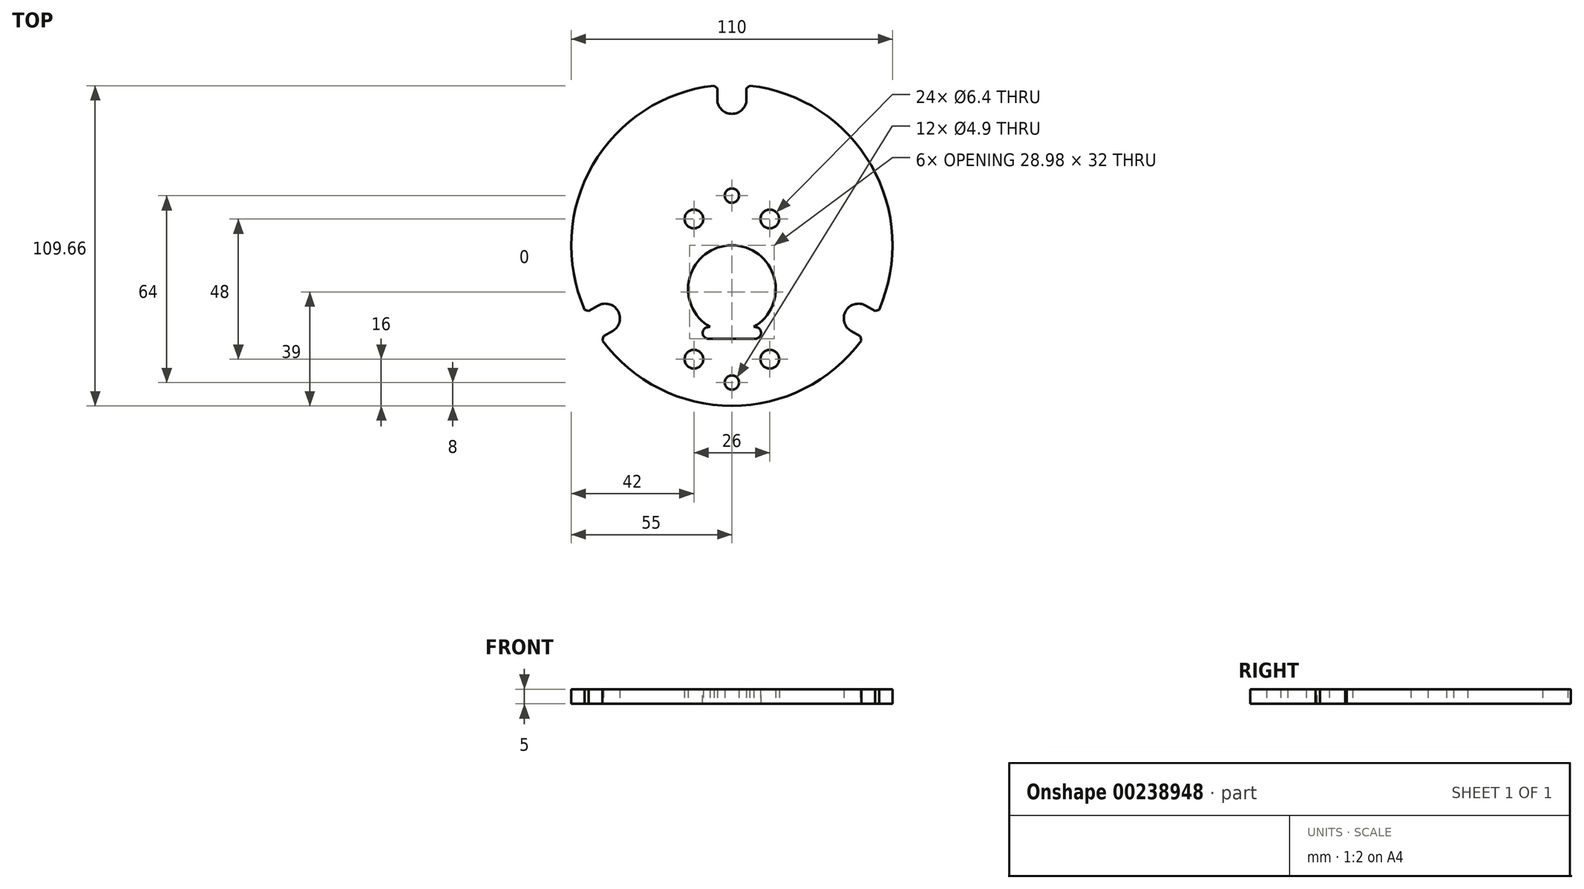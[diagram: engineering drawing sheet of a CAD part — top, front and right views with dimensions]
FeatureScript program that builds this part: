
annotation { "Feature Type Name" : "Feature", "Feature Type Description" : "" }
export const myFeature = defineFeature(function(context is Context, id is Id, definition is map)
    precondition{}
    {
        {
            var Q0;
            Q0=qCreatedBy(makeId("Top.planeOp"),FACE);
            var sketch = newSketch(context, id + "F0", { "sketchPlane" : qUnion([Q0])});
            skCircle(sketch, "E0", {"center": v(0, 0) * mm, "radius": 95 * mm, "construction": true});
            skPoint(sketch, "E1", {"position": v(0, -15) * mm});
            skPoint(sketch, "E2", {"position": v(0, 15) * mm});
            skCircle(sketch, "E3", {"center": v(0, 15) * mm, "radius": 80 * mm, "construction": true});
            skCircle(sketch, "E4", {"center": v(0, 15) * mm, "radius": 70 * mm, "construction": true});
            skLineSegment(sketch, "E5", {"start": v(0, 15) * mm, "end": v(-99.15, 72.25) * mm, "construction": true});
            skLineSegment(sketch, "E6.MirrorCS", {"start": v(0, 15) * mm, "end": v(99.15, 72.25) * mm, "construction": true});
            skArc(sketch, "E7.1.0", {"start": v(40.59, 44.2) * mm, "mid": v(7.54, 64.43) * mm, "end": v(-30.04, 54.97) * mm, "construction": true});
            skArc(sketch, "E8.trimOffspring", {"start": v(50.4, -7.04) * mm, "mid": v(47.63, 42.5) * mm, "end": v(6.11, 69.66) * mm});
            skArc(sketch, "E9.trimOffspring", {"start": v(-46.91, 32.3) * mm, "mid": v(1.75, -34.97) * mm, "end": v(45.58, 35.55) * mm, "construction": true});
            skCircle(sketch, "E10", {"center": v(0, 0) * mm, "radius": 15 * mm});
            skArc(sketch, "E11", {"start": v(-5, 65) * mm, "mid": v(0, 60) * mm, "end": v(5, 65) * mm});
            skLineSegment(sketch, "E12", {"start": v(5, 68.67) * mm, "end": v(5, 64.75) * mm});
            skLineSegment(sketch, "E13", {"start": v(-5, 68.67) * mm, "end": v(-5, 64.75) * mm});
            skArc(sketch, "E14.trimOffspring", {"start": v(-6.11, 69.66) * mm, "mid": v(-47.36, 42.97) * mm, "end": v(-50.82, -6.03) * mm});
            skLineSegment(sketch, "E15", {"start": v(-6.11, 69.66) * mm, "end": v(-5, 68.67) * mm});
            skLineSegment(sketch, "E16", {"start": v(6.11, 69.66) * mm, "end": v(5, 68.67) * mm});
            skCircle(sketch, "E17", {"center": v(0, 65) * mm, "radius": 5 * mm, "construction": true});
            skCircle(sketch, "E18", {"center": v(0, 65) * mm, "radius": 8.5 * mm, "construction": true});
            skCircle(sketch, "E19", {"center": v(0, 65) * mm, "radius": 20 * mm, "construction": true});
            skCircle(sketch, "E20.1.0", {"center": v(-43.3, -10) * mm, "radius": 8.5 * mm, "construction": true});
            skPoint(sketch, "E20.1.1", {"position": v(-43.3, -10) * mm});
            skCircle(sketch, "E20.1.2", {"center": v(-43.3, -10) * mm, "radius": 5 * mm, "construction": true});
            skLineSegment(sketch, "E20.1.3", {"start": v(-43.98, -16.16) * mm, "end": v(-40.58, -14.2) * mm});
            skArc(sketch, "E20.1.4", {"start": v(-40.8, -14.33) * mm, "mid": v(-38.97, -7.5) * mm, "end": v(-45.8, -5.67) * mm});
            skLineSegment(sketch, "E20.1.5", {"start": v(-44.28, -17.62) * mm, "end": v(-43.98, -16.16) * mm});
            skLineSegment(sketch, "E20.1.6", {"start": v(-48.98, -7.5) * mm, "end": v(-45.58, -5.54) * mm});
            skLineSegment(sketch, "E20.1.7", {"start": v(-50.4, -7.04) * mm, "end": v(-48.98, -7.5) * mm});
            skCircle(sketch, "E20.1.8", {"center": v(-43.3, -10) * mm, "radius": 20 * mm, "construction": true});
            skCircle(sketch, "E20.2.0", {"center": v(43.3, -10) * mm, "radius": 8.5 * mm, "construction": true});
            skPoint(sketch, "E20.2.1", {"position": v(43.3, -10) * mm});
            skCircle(sketch, "E20.2.2", {"center": v(43.3, -10) * mm, "radius": 5 * mm, "construction": true});
            skLineSegment(sketch, "E20.2.3", {"start": v(48.98, -7.5) * mm, "end": v(45.58, -5.54) * mm});
            skArc(sketch, "E20.2.4", {"start": v(45.8, -5.67) * mm, "mid": v(38.97, -7.5) * mm, "end": v(40.8, -14.33) * mm});
            skLineSegment(sketch, "E20.2.5", {"start": v(50.4, -7.04) * mm, "end": v(48.98, -7.5) * mm});
            skLineSegment(sketch, "E20.2.6", {"start": v(43.98, -16.16) * mm, "end": v(40.58, -14.2) * mm});
            skLineSegment(sketch, "E20.2.7", {"start": v(44.28, -17.62) * mm, "end": v(43.98, -16.16) * mm});
            skCircle(sketch, "E20.2.8", {"center": v(43.3, -10) * mm, "radius": 20 * mm, "construction": true});
            skArc(sketch, "E21.trimOffspring", {"start": v(-50.82, -6.03) * mm, "mid": v(-50.6, -6.54) * mm, "end": v(-50.4, -7.04) * mm});
            skArc(sketch, "E22.trimOffspring", {"start": v(-44.28, -17.62) * mm, "mid": v(0, -40) * mm, "end": v(44.28, -17.62) * mm});
            skCircle(sketch, "E23", {"center": v(0, 0) * mm, "radius": 55 * mm, "construction": true});
            skCircle(sketch, "E24", {"center": v(0, 0) * mm, "radius": 40 * mm, "construction": true});
            skCircle(sketch, "E25", {"center": v(0, 0) * mm, "radius": 33.5 * mm, "construction": true});
            skLineSegment(sketch, "E26", {"start": v(-13, 12.1) * mm, "end": v(-13, -37.02) * mm, "construction": true});
            skLineSegment(sketch, "E27", {"start": v(-31.23, -24) * mm, "end": v(-2.5, -24) * mm, "construction": true});
            skLineSegment(sketch, "E28", {"start": v(-31.23, -32) * mm, "end": v(8.76, -32) * mm, "construction": true});
            skCircle(sketch, "E29", {"center": v(-13, -24) * mm, "radius": 3.2 * mm});
            skCircle(sketch, "E30", {"center": v(0, -32) * mm, "radius": 2.45 * mm});
            skCircle(sketch, "E31.MirrorC", {"center": v(13, -24) * mm, "radius": 3.2 * mm});
            skCircle(sketch, "E32.MirrorC", {"center": v(-13, 24) * mm, "radius": 3.2 * mm});
            skCircle(sketch, "E33.MirrorC", {"center": v(13, 24) * mm, "radius": 3.2 * mm});
            skCircle(sketch, "E34.MirrorC", {"center": v(0, 32) * mm, "radius": 2.45 * mm});
            skCircle(sketch, "E35", {"center": v(0, 0) * mm, "radius": 12.5 * mm, "construction": true});
            skSolve(sketch);
        }
        {
            var Q0;
            Q0=qSketchRegion(id+"F0",true);
            extrude(context, id + "F1", {"entities" : qUnion([Q0]), "depth" : 12 * mm, "hasSecondDirection" : true, "secondDirectionOppositeDirection" : false, "secondDirectionDepth" : 7 * mm});
        }
        {
            var Q0;
            Q0=qCreatedBy(makeId("Top.planeOp"),FACE);
            var sketch = newSketch(context, id + "F2", { "sketchPlane" : qUnion([Q0])});
            skCircle(sketch, "E36.0", {"center": v(0, 0) * mm, "radius": 12.5 * mm, "construction": true});
            skLineSegment(sketch, "E37", {"start": v(-12.89, -12.5) * mm, "end": v(0, -12.5) * mm, "construction": true});
            skLineSegment(sketch, "E38", {"start": v(-8, -13) * mm, "end": v(0, -13) * mm});
            skLineSegment(sketch, "E39", {"start": v(-8, -8.9) * mm, "end": v(-8, -21.1) * mm, "construction": true});
            skArc(sketch, "E40", {"start": v(-8, -13) * mm, "mid": v(-10, -15) * mm, "end": v(-8, -17) * mm});
            skLineSegment(sketch, "E41", {"start": v(-8, -17) * mm, "end": v(0, -17) * mm});
            skPoint(sketch, "E42.orphan", {"position": v(0, -5.52) * mm});
            skLineSegment(sketch, "E43.MirrorCS", {"start": v(8, -13) * mm, "end": v(0, -13) * mm});
            skArc(sketch, "E44.MirrorCS", {"start": v(8, -13) * mm, "mid": v(10, -15) * mm, "end": v(8, -17) * mm});
            skLineSegment(sketch, "E45.MirrorCS", {"start": v(8, -17) * mm, "end": v(0, -17) * mm});
            skCircle(sketch, "E46.0", {"center": v(0, 0) * mm, "radius": 15 * mm, "construction": true});
            skSolve(sketch);
        }
        {
            var Q0;
            Q0=qSketchRegion(id+"F2",true);
            extrude(context, id + "F3", {"entities" : qUnion([Q0]), "operationType" : NewBodyOperationType.REMOVE, "oppositeDirection" : true, "depth" : 40 * mm, "hasSecondDirection" : true, "secondDirectionOppositeDirection" : false, "secondDirectionDepth" : 40 * mm});
        }
    });
